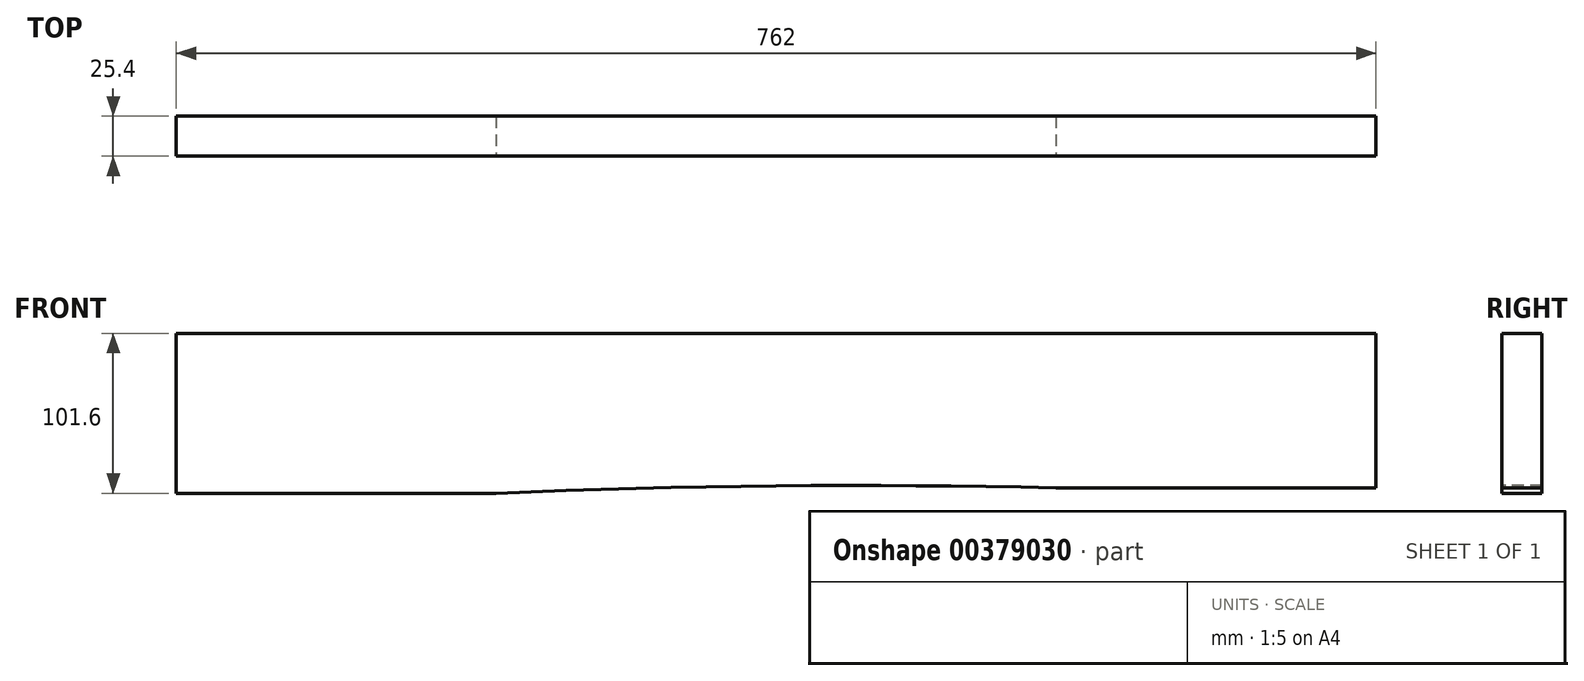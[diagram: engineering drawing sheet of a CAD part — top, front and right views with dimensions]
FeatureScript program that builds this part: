
annotation { "Feature Type Name" : "Feature", "Feature Type Description" : "" }
export const myFeature = defineFeature(function(context is Context, id is Id, definition is map)
    precondition{}
    {
        {
            var Q0;
            Q0=qCreatedBy(makeId("Front.planeOp"),FACE);
            var sketch = newSketch(context, id + "F0", { "sketchPlane" : qUnion([Q0])});
            skLineSegment(sketch, "E0", {"start": v(-381, 66.26) * mm, "end": v(381, 66.26) * mm});
            skLineSegment(sketch, "E1", {"start": v(-381, 66.26) * mm, "end": v(-381, -35.34) * mm});
            skLineSegment(sketch, "E2", {"start": v(381, 66.26) * mm, "end": v(381, -31.9) * mm});
            skLineSegment(sketch, "E3", {"start": v(-177.8, -35.34) * mm, "end": v(-381, -35.34) * mm});
            skLineSegment(sketch, "E4", {"start": v(381, -31.9) * mm, "end": v(177.8, -31.9) * mm});
            skArc(sketch, "E5", {"start": v(177.8, -31.9) * mm, "mid": v(-0.03, -30.66) * mm, "end": v(-177.8, -35.34) * mm});
            skSolve(sketch);
        }
        {
            var Q0;
            Q0 = qSketchRegion(id + "F0", true);
            extrude(context, id + "F1", {"entities" : qUnion([Q0]), "oppositeDirection" : true, "depth" : 25.4 * mm});
        }
    });
